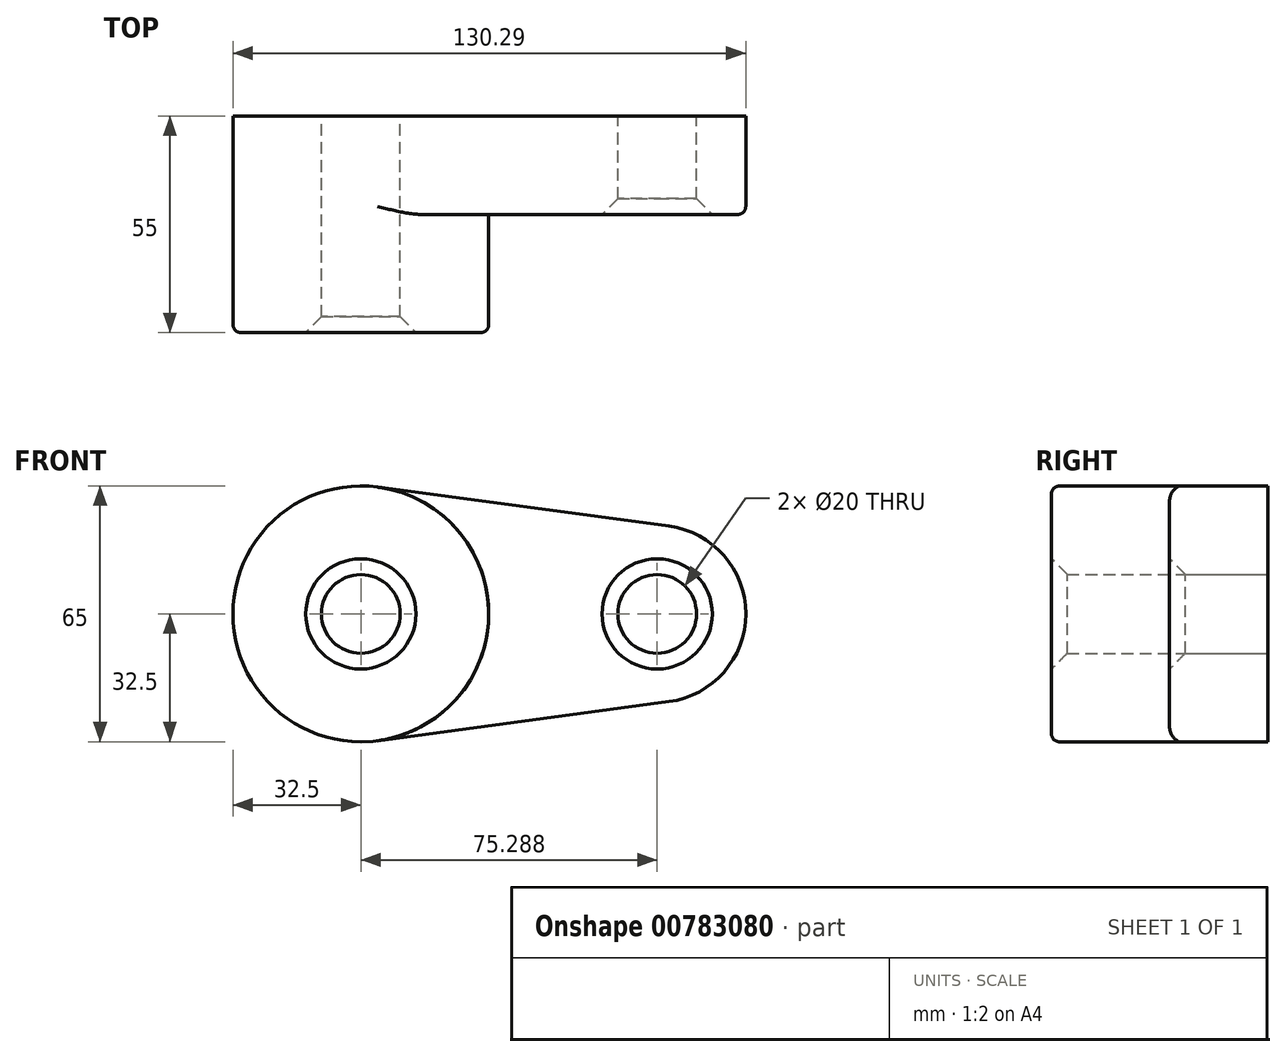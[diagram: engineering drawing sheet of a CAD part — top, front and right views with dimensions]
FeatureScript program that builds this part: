
annotation { "Feature Type Name" : "Feature", "Feature Type Description" : "" }
export const myFeature = defineFeature(function(context is Context, id is Id, definition is map)
    precondition{}
    {
        {
            var Q0;
            Q0=qCreatedBy(makeId("Front.planeOp"),FACE);
            var sketch = newSketch(context, id + "F0", { "sketchPlane" : qUnion([Q0])});
            skCircle(sketch, "E0", {"center": v(0, 0) * mm, "radius": 32.5 * mm});
            skCircle(sketch, "E1", {"center": v(75.29, 0) * mm, "radius": 22.5 * mm});
            skLineSegment(sketch, "E2", {"start": v(4.32, 32.21) * mm, "end": v(78.28, 22.3) * mm});
            skLineSegment(sketch, "E3", {"start": v(4.32, -32.21) * mm, "end": v(78.28, -22.3) * mm});
            skCircle(sketch, "E4", {"center": v(0, 0) * mm, "radius": 10 * mm});
            skCircle(sketch, "E5", {"center": v(75.29, 0) * mm, "radius": 10 * mm});
            skSolve(sketch);
        }
        {
            var Q0;
            Q0 = qSketchRegion(id + "F0", true);
            extrude(context, id + "F1", {"entities" : qUnion([Q0]), "depth" : 25 * mm, "offsetDistance" : 25 * mm});
        }
        {
            var Q0;
            Q0=makeQuery(id+"F0.imprint","IMPRINT",FACE,{"disambiguationData":[TD([[makeQuery(id+"F0.imprint","IMPRINT",EDGE,{"derivedFrom":sQuery(id+"F0.wireOp",EDGE,"E4")}),-1.0]])]});
            extrude(context, id + "F2", {"entities" : qUnion([Q0]), "operationType" : NewBodyOperationType.ADD, "depth" : 55 * mm, "offsetDistance" : 25 * mm});
        }
        {
            var Q0;
            Q0=makeQuery(id+"F2.opExtrude","CAP_EDGE",EDGE,{"disambiguationData":[OSD([sQuery(id+"F0.wireOp",EDGE,"E0")])],"isStart":false});
            var Q1;
            Q1=makeQuery(id+"F1.opExtrude","CAP_EDGE",EDGE,{"disambiguationData":[OSD([sQuery(id+"F0.wireOp",EDGE,"E1")])],"isStart":false});
            fillet(context, id + "F3", {"entities" : qUnion([Q0, Q1]), "radius" : 2 * mm, "tangentPropagation" : true, "allowEdgeOverflow" : false});
        }
        {
            var Q0;
            Q0=makeQuery(id+"F2.opExtrude","CAP_EDGE",EDGE,{"disambiguationData":[OSD([sQuery(id+"F0.wireOp",EDGE,"E4")])],"isStart":false});
            var Q1;
            Q1=makeQuery(id+"F1.opExtrude","CAP_EDGE",EDGE,{"disambiguationData":[OSD([sQuery(id+"F0.wireOp",EDGE,"E5")])],"isStart":false});
            chamfer(context, id + "F4", {"entities" : qUnion([Q0, Q1]), "width" : 4 * mm, "tangentPropagation" : true});
        }
    });
